# Revit family: NBS_Allermuir_OffcChrs-en-us-Cardita_Stool
name_source: partatom
category: Furniture
revit_build: Autodesk Revit 2018 (Build: 20190510_1515(x64)
units: mm (PartAtom-declared; Revit-internal decimal feet)

## family parameters
Always vertical = Yes
Cut with Voids When Loaded = No
Room Calculation Point = No
Shared = No
Work Plane-Based = No

## types (2) — shared parameters
AssetType = Movable
Category = Pr_40_50_12_57:Office chairs
Color = Solid Ash, White Oak stain, American Cherry stain, American Walnut stain, Dark Walnut stain, Wenge stain, White as Snow color wash, Back to Black colour wash, Slate Gray color wash, Smoke Gray color wash, Vintage Red color wash, Ruby Red color wash, Fern Green color wash, Peacock Green color wash, Blue Skies color wash, Sapphire Blue color wash, Orange Crush color wash, Mellow Yellow color wash, Nut Brown color wash, Turtle Dove color wash, Sherbert Yellow color wash, Blush Pink color wash
Description = High stool on wood legs
DurationUnit = year
ExpectedLife = 10
Features = Molded shell, Fully upholstered with luxury quilt detail, Solid Ash legs with a clear finish, Footrest finished in Polished Chrome, Plastic glides, Solid Ash legs can be stained or colorwashed, Plastic glides with felt
Finish = Clear Solid Ash
FootrestMaterial = NBS_Allermuir_Chrome_Polished
FrameFinish = Clear
FrameMaterial = Solid Ash
IfcExportAs = IfcFurnitureType
IfcExportType = STOOL
IsBuiltIn = No
LegMaterial = NBS_Allermuir_Ash_ClearFinish
ManufacturerName = Allermuir
ManufacturerURL = www.allermuir.com
Material = Fabric, PU Foam, Steel, Solid Wood
ModelReference = Cardita_Stool
NBSCertification = www.nationalbimlibrary.com/cert/d3t3ifra
NBSDescription = Office chairs
NBSReference = 45-35-20/330
NominalDepth = 20 "
NominalLength = 20 "
NominalWidth = 20 "
OmniClassCode = 22-12 52 23
OmniClassTitle = Office Seating
OmniClassVersion = Table 22 2012-05-16
ProductInformation = https://www.allermuir.com
SeatDepth = 14.5"
SeatMaterial = NBS_Allermuir_Fabric
SeatWidth = 17.25"
Status = UNSET
Style = Stool
SustainabilityPerformance = 99% recyclable
Uniclass2015Code = Pr_40_50_12_57
Uniclass2015Title = Office chairs
Uniclass2015Version = Products v1.15
Version = 1
WarrantyDescription = Allermuir warrant that its manufactured products are free from manufacturing defects - in materials or workmanship - for a period of ten (10) years. , Allermuir will repair, or replace (at Allermuir's sole discretion) with comparable free of charge materials / components, any product / component which fails under normal use in a single shift environment, as a result of a defect in the materials and/ or workmanship
WarrantyDurationParts = 10
WarrantyDurationUnit = year
WoodStains = White Oak, American Cherry, American Walnut, Dark walnut, Wenge
zero-valued in all types: HighestSeatingHeight, LowestSeatingHeight

## per-type parameters (varying)
| type | BIMObjectName | FootrestHeight | ModelNumber | Name | NominalHeight | SeatingHeight | Size |
| Cardita_Stool_CRD03 | NBS_Allermuir_OfficeChairs_Cardita_Stool_CRD03-US | 11 " | CRD03 | OfficeChairs_CRD03_Cardita_Allermuir | 40 " | 29 " | 20.25 x 39.75 x 19.75" |
| Cardita_Stool_CRD03CH | NBS_Allermuir_OfficeChairs_Cardita_Stool_CRD03CH-US | 9 " | CRD03CH | OfficeChairs_CRD03CH_Cardita_Allermuir | 35 " | 24 " | 20.25 x 34.75 x 19.75" |

## geometry (parser evidence)
native form markers: Sweep x5
no freeform markers — native parametric forms only
